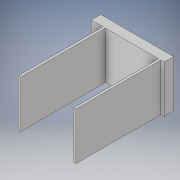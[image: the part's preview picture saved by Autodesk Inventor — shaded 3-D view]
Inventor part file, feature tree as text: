
AUTODESK INVENTOR PART (.ipt)
format: ipt  version: 2017 (Build 210142000, 142)  size: 111,616 bytes
history: native  units: in
note: dims shown in document units (in); Inventor stores cm internally (conversion verified against a paired STEP export)
features: extrude x3, sketch x3
ambient origin geometry x8: Origin, YZ Plane, XZ Plane, XY Plane, X Axis, Y Axis, Z Axis, Center Point
bodies: Solid1 (feature_tree)
feature tree (6):
  extrude  "Extrusion1"  Depth=2.5in
  extrude  "Extrusion2"  Depth=0.3in
  extrude  "Extrusion3"  Depth=4.5in TaperAngle=0.0deg
  sketch  "Sketch1"  dims[d0=3.865in d1=2.5in]
  sketch  "Sketch2"  dims[d2=0.5in d3=0.0in d4=0.3in]
  sketch  "Sketch3"  dims[d5=0.125in d6=4.5in d7=0.0in d8=0.625in d9=0.125in d10=4.5in d11=0.0in]
